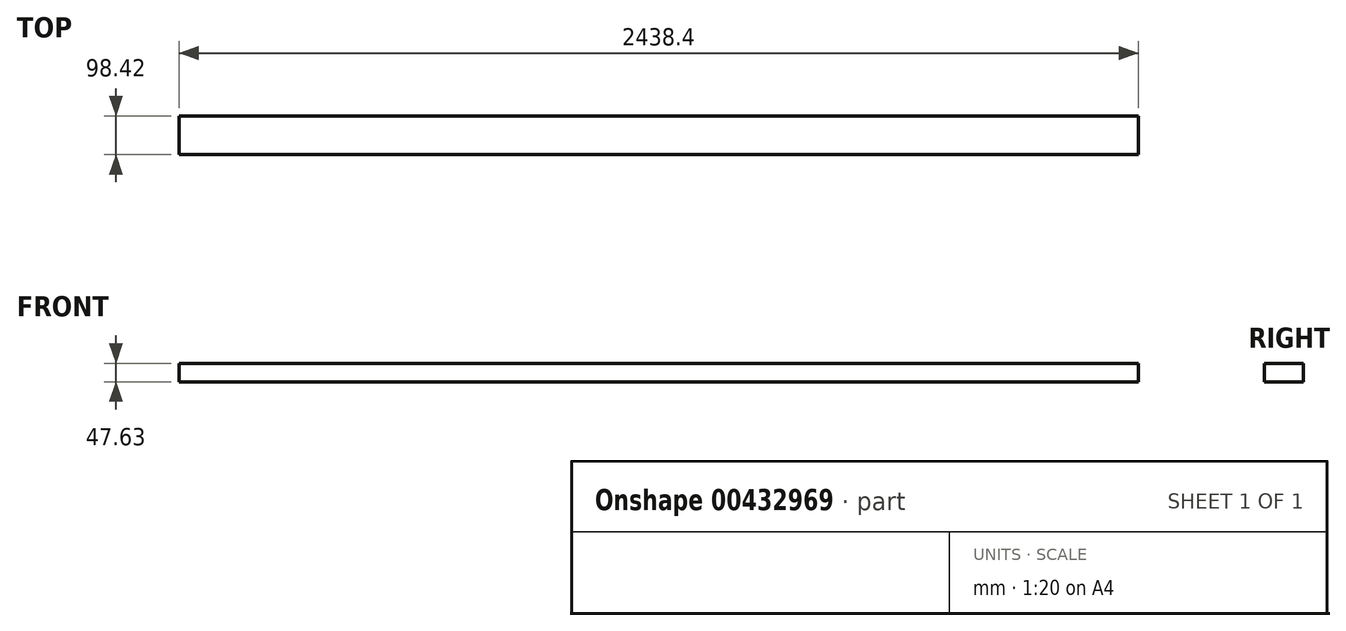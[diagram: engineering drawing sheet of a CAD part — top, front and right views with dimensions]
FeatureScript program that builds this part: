
annotation { "Feature Type Name" : "Feature", "Feature Type Description" : "" }
export const myFeature = defineFeature(function(context is Context, id is Id, definition is map)
    precondition{}
    {
        {
            var Q0;
            Q0=qCreatedBy(makeId("Front.planeOp"),FACE);
            var sketch = newSketch(context, id + "F0", { "sketchPlane" : qUnion([Q0])});
            skLineSegment(sketch, "E0.bottom", {"start": v(-423.2, 1030) * mm, "end": v(2015.2, 1030) * mm});
            skLineSegment(sketch, "E0.top", {"start": v(-423.2, 982.38) * mm, "end": v(2015.2, 982.38) * mm});
            skLineSegment(sketch, "E0.left", {"start": v(-423.2, 1030) * mm, "end": v(-423.2, 982.38) * mm});
            skLineSegment(sketch, "E0.right", {"start": v(2015.2, 1030) * mm, "end": v(2015.2, 982.38) * mm});
            skLineSegment(sketch, "E1.bottom", {"start": v(-423.2, 982.38) * mm, "end": v(-375.57, 982.38) * mm});
            skLineSegment(sketch, "E1.top", {"start": v(-423.2, -236.82) * mm, "end": v(-375.57, -236.82) * mm});
            skLineSegment(sketch, "E1.left", {"start": v(-423.2, 982.38) * mm, "end": v(-423.2, -236.82) * mm});
            skLineSegment(sketch, "E1.right", {"start": v(-375.57, 982.38) * mm, "end": v(-375.57, -236.82) * mm});
            skLineSegment(sketch, "E2.bottom", {"start": v(2015.2, 982.38) * mm, "end": v(1967.58, 982.38) * mm});
            skLineSegment(sketch, "E2.top", {"start": v(2015.2, -236.82) * mm, "end": v(1967.58, -236.82) * mm});
            skLineSegment(sketch, "E2.left", {"start": v(2015.2, 982.38) * mm, "end": v(2015.2, -236.82) * mm});
            skLineSegment(sketch, "E2.right", {"start": v(1967.58, 982.38) * mm, "end": v(1967.58, -236.82) * mm});
            skSolve(sketch);
        }
        {
            var Q0;
            Q0=makeQuery(id+"F0.imprint","IMPRINT",FACE,{"disambiguationData":[TD([[makeQuery(id+"F0.imprint","IMPRINT",EDGE,{"derivedFrom":sQuery(id+"F0.wireOp",EDGE,"E1.bottom")}),-1.0]])]});
            var Q1;
            Q1=makeQuery(id+"F0.imprint","IMPRINT",FACE,{"disambiguationData":[TD([[makeQuery(id+"F0.imprint","IMPRINT",EDGE,{"derivedFrom":sQuery(id+"F0.wireOp",EDGE,"E0.bottom")}),-1.0]])]});
            var Q2;
            Q2=makeQuery(id+"F0.imprint","IMPRINT",FACE,{"disambiguationData":[TD([[makeQuery(id+"F0.imprint","IMPRINT",EDGE,{"derivedFrom":sQuery(id+"F0.wireOp",EDGE,"E2.bottom")}),1.0]])]});
            extrude(context, id + "F1", {"entities" : qUnion([Q0, Q1, Q2]), "depth" : 98.42 * mm});
        }
    });
